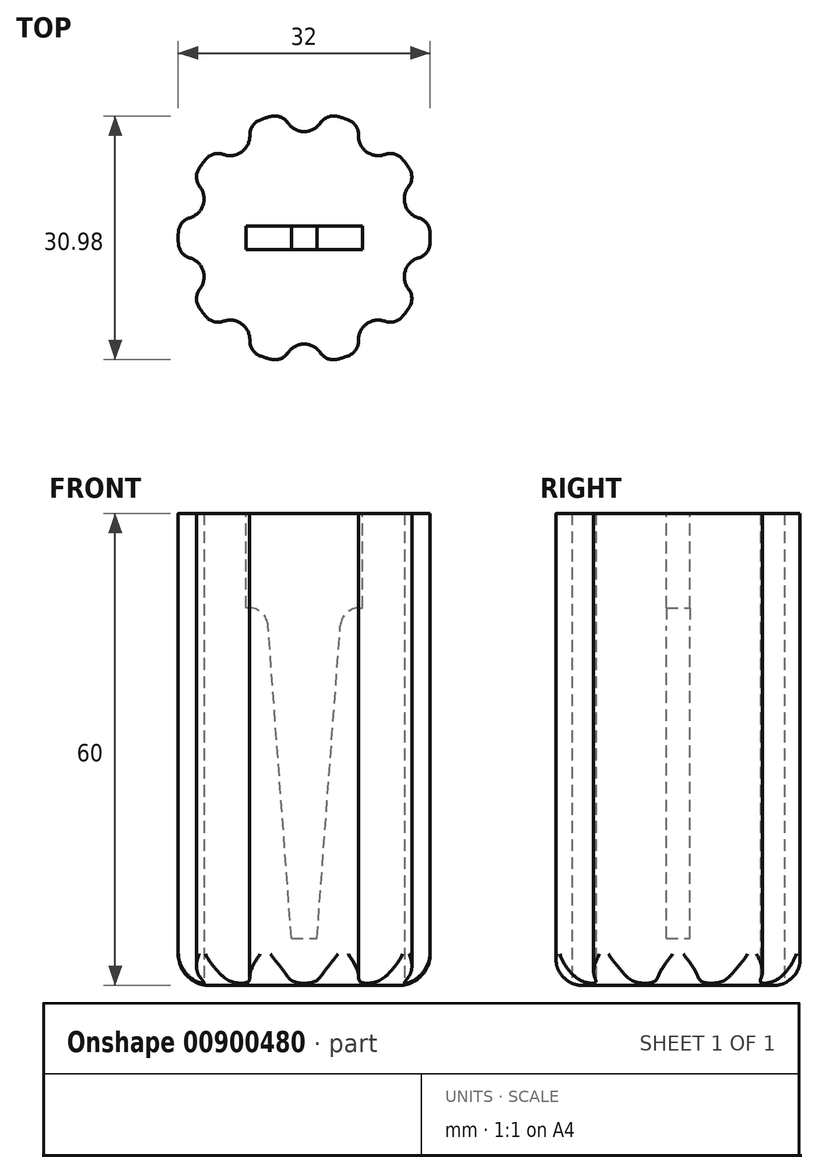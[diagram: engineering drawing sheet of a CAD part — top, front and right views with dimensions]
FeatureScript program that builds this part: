
annotation { "Feature Type Name" : "Feature", "Feature Type Description" : "" }
export const myFeature = defineFeature(function(context is Context, id is Id, definition is map)
    precondition{}
    {
        {
            var Q0;
            Q0=qCreatedBy(makeId("Top.planeOp"),FACE);
            var sketch = newSketch(context, id + "F0", { "sketchPlane" : qUnion([Q0])});
            skArc(sketch, "E0", {"start": v(-4.27, 15.42) * mm, "mid": v(-4.94, 15.22) * mm, "end": v(-5.6, 14.98) * mm});
            skArc(sketch, "E1", {"start": v(-2.08, 14.6) * mm, "mid": v(0, 13.5) * mm, "end": v(2.08, 14.6) * mm});
            skPoint(sketch, "E2.visualSharp", {"position": v(-2.5, 15.8) * mm});
            skArc(sketch, "E2.filletArc", {"start": v(-2.08, 14.6) * mm, "mid": v(-3.04, 15.37) * mm, "end": v(-4.27, 15.42) * mm});
            skPoint(sketch, "E3.visualSharp", {"position": v(2.5, 15.8) * mm});
            skArc(sketch, "E3.filletArc", {"start": v(4.27, 15.42) * mm, "mid": v(3.04, 15.37) * mm, "end": v(2.08, 14.6) * mm});
            skArc(sketch, "E4.1.0", {"start": v(-10.26, 10.6) * mm, "mid": v(-11.5, 10.64) * mm, "end": v(-12.52, 9.96) * mm});
            skArc(sketch, "E4.1.1", {"start": v(-10.26, 10.6) * mm, "mid": v(-7.94, 10.92) * mm, "end": v(-6.9, 13.04) * mm});
            skArc(sketch, "E4.1.2", {"start": v(-5.6, 14.98) * mm, "mid": v(-6.57, 14.22) * mm, "end": v(-6.9, 13.04) * mm});
            skArc(sketch, "E4.2.0", {"start": v(-14.53, 2.54) * mm, "mid": v(-15.56, 1.86) * mm, "end": v(-15.98, 0.7) * mm});
            skArc(sketch, "E4.2.1", {"start": v(-14.53, 2.54) * mm, "mid": v(-12.84, 4.17) * mm, "end": v(-13.25, 6.49) * mm});
            skArc(sketch, "E4.2.2", {"start": v(-13.35, 8.83) * mm, "mid": v(-13.68, 7.64) * mm, "end": v(-13.25, 6.49) * mm});
            skArc(sketch, "E4.3.0", {"start": v(-13.25, -6.49) * mm, "mid": v(-13.68, -7.64) * mm, "end": v(-13.35, -8.83) * mm});
            skArc(sketch, "E4.3.1", {"start": v(-13.25, -6.49) * mm, "mid": v(-12.84, -4.17) * mm, "end": v(-14.53, -2.54) * mm});
            skArc(sketch, "E4.3.2", {"start": v(-15.98, -0.7) * mm, "mid": v(-15.56, -1.86) * mm, "end": v(-14.53, -2.54) * mm});
            skArc(sketch, "E4.4.0", {"start": v(-6.9, -13.04) * mm, "mid": v(-6.57, -14.22) * mm, "end": v(-5.6, -14.98) * mm});
            skArc(sketch, "E4.4.1", {"start": v(-6.9, -13.04) * mm, "mid": v(-7.94, -10.92) * mm, "end": v(-10.26, -10.6) * mm});
            skArc(sketch, "E4.4.2", {"start": v(-12.52, -9.96) * mm, "mid": v(-11.5, -10.64) * mm, "end": v(-10.26, -10.6) * mm});
            skArc(sketch, "E4.5.0", {"start": v(2.08, -14.6) * mm, "mid": v(3.04, -15.37) * mm, "end": v(4.27, -15.42) * mm});
            skArc(sketch, "E4.5.1", {"start": v(2.08, -14.6) * mm, "mid": v(0, -13.5) * mm, "end": v(-2.08, -14.6) * mm});
            skArc(sketch, "E4.5.2", {"start": v(-4.27, -15.42) * mm, "mid": v(-3.04, -15.37) * mm, "end": v(-2.08, -14.6) * mm});
            skArc(sketch, "E4.6.0", {"start": v(10.26, -10.6) * mm, "mid": v(11.5, -10.64) * mm, "end": v(12.52, -9.96) * mm});
            skArc(sketch, "E4.6.1", {"start": v(10.26, -10.6) * mm, "mid": v(7.94, -10.92) * mm, "end": v(6.9, -13.04) * mm});
            skArc(sketch, "E4.6.2", {"start": v(5.6, -14.98) * mm, "mid": v(6.57, -14.22) * mm, "end": v(6.9, -13.04) * mm});
            skArc(sketch, "E4.7.0", {"start": v(14.53, -2.54) * mm, "mid": v(15.56, -1.86) * mm, "end": v(15.98, -0.7) * mm});
            skArc(sketch, "E4.7.1", {"start": v(14.53, -2.54) * mm, "mid": v(12.84, -4.17) * mm, "end": v(13.25, -6.49) * mm});
            skArc(sketch, "E4.7.2", {"start": v(13.35, -8.83) * mm, "mid": v(13.68, -7.64) * mm, "end": v(13.25, -6.49) * mm});
            skArc(sketch, "E4.8.0", {"start": v(13.25, 6.49) * mm, "mid": v(13.68, 7.64) * mm, "end": v(13.35, 8.83) * mm});
            skArc(sketch, "E4.8.1", {"start": v(13.25, 6.49) * mm, "mid": v(12.84, 4.17) * mm, "end": v(14.53, 2.54) * mm});
            skArc(sketch, "E4.8.2", {"start": v(15.98, 0.7) * mm, "mid": v(15.56, 1.86) * mm, "end": v(14.53, 2.54) * mm});
            skArc(sketch, "E4.9.0", {"start": v(6.9, 13.04) * mm, "mid": v(6.57, 14.22) * mm, "end": v(5.6, 14.98) * mm});
            skArc(sketch, "E4.9.1", {"start": v(6.9, 13.04) * mm, "mid": v(7.94, 10.92) * mm, "end": v(10.26, 10.6) * mm});
            skArc(sketch, "E4.9.2", {"start": v(12.52, 9.96) * mm, "mid": v(11.5, 10.64) * mm, "end": v(10.26, 10.6) * mm});
            skArc(sketch, "E5.trimOffspring", {"start": v(-15.98, 0.7) * mm, "mid": v(-16, 0) * mm, "end": v(-15.98, -0.7) * mm});
            skArc(sketch, "E6.trimOffspring", {"start": v(-12.52, 9.96) * mm, "mid": v(-12.94, 9.4) * mm, "end": v(-13.35, 8.83) * mm});
            skArc(sketch, "E7.trimOffspring", {"start": v(5.6, 14.98) * mm, "mid": v(4.94, 15.22) * mm, "end": v(4.27, 15.42) * mm});
            skArc(sketch, "E8.trimOffspring", {"start": v(13.35, 8.83) * mm, "mid": v(12.94, 9.4) * mm, "end": v(12.52, 9.96) * mm});
            skArc(sketch, "E9.trimOffspring", {"start": v(15.98, -0.7) * mm, "mid": v(16, 0) * mm, "end": v(15.98, 0.7) * mm});
            skArc(sketch, "E10.trimOffspring", {"start": v(12.52, -9.96) * mm, "mid": v(12.94, -9.4) * mm, "end": v(13.35, -8.83) * mm});
            skArc(sketch, "E11.trimOffspring", {"start": v(4.27, -15.42) * mm, "mid": v(4.94, -15.22) * mm, "end": v(5.6, -14.98) * mm});
            skArc(sketch, "E12.trimOffspring", {"start": v(-5.6, -14.98) * mm, "mid": v(-4.94, -15.22) * mm, "end": v(-4.27, -15.42) * mm});
            skArc(sketch, "E13.trimOffspring", {"start": v(-13.35, -8.83) * mm, "mid": v(-12.94, -9.4) * mm, "end": v(-12.52, -9.96) * mm});
            skSolve(sketch);
        }
        {
            var Q0;
            Q0=makeQuery(id+"F0.imprint","IMPRINT",FACE,{"disambiguationData":[TD([[makeQuery(id+"F0.imprint","IMPRINT",EDGE,{"derivedFrom":sQuery(id+"F0.wireOp",EDGE,"E0")}),1.0]])]});
            extrude(context, id + "F1", {"entities" : qUnion([Q0]), "depth" : 60 * mm, "offsetDistance" : 25.4 * mm});
        }
        {
            var Q0;
            Q0=qCreatedBy(makeId("Right.planeOp"),FACE);
            var sketch = newSketch(context, id + "F2", { "sketchPlane" : qUnion([Q0])});
            skLineSegment(sketch, "E14.bottom", {"start": v(12, 0) * mm, "end": v(16, 0) * mm});
            skLineSegment(sketch, "E14.top", {"start": v(12, 4) * mm, "end": v(16, 4) * mm});
            skLineSegment(sketch, "E14.left", {"start": v(12, 0) * mm, "end": v(12, 4) * mm});
            skLineSegment(sketch, "E14.right", {"start": v(16, 0) * mm, "end": v(16, 4) * mm});
            skArc(sketch, "E15", {"start": v(12, 0) * mm, "mid": v(14.83, 1.17) * mm, "end": v(16, 4) * mm});
            skLineSegment(sketch, "E16", {"start": v(12, 0) * mm, "end": v(0, 0) * mm});
            skLineSegment(sketch, "E17", {"start": v(0, 0) * mm, "end": v(0, 89.76) * mm});
            skSolve(sketch);
        }
        {
            var Q0;
            Q0=makeQuery(id+"F2.imprint","IMPRINT",FACE,{"disambiguationData":[TD([[makeQuery(id+"F2.imprint","IMPRINT",EDGE,{"derivedFrom":sQuery(id+"F2.wireOp",EDGE,"E14.bottom")}),1.0]])]});
            var Q1;
            Q1=sQuery(id+"F2.wireOp",EDGE,"E17");
            revolve(context, id + "F3", {"operationType" : NewBodyOperationType.REMOVE, "surfaceOperationType" : NewSurfaceOperationType.NEW, "entities" : qUnion([Q0]), "axis" : qUnion([Q1]), "revolveType" : RevolveType.FULL, "oppositeDirection" : true});
        }
        {
            var Q0;
            Q0=qCreatedBy(makeId("Front.planeOp"),FACE);
            var sketch = newSketch(context, id + "F4", { "sketchPlane" : qUnion([Q0])});
            skLineSegment(sketch, "E18", {"start": v(0, 0) * mm, "end": v(0, 6) * mm});
            skLineSegment(sketch, "E19", {"start": v(0, 6) * mm, "end": v(0, 48) * mm});
            skLineSegment(sketch, "E20", {"start": v(0, 48) * mm, "end": v(0, 60) * mm});
            skLineSegment(sketch, "E21.bottom", {"start": v(7.07, 48) * mm, "end": v(7.4, 48) * mm});
            skLineSegment(sketch, "E21.top", {"start": v(0, 60) * mm, "end": v(7.4, 60) * mm});
            skLineSegment(sketch, "E21.right", {"start": v(7.4, 48) * mm, "end": v(7.4, 60) * mm});
            skLineSegment(sketch, "E22", {"start": v(0, 6) * mm, "end": v(1.63, 6) * mm});
            skLineSegment(sketch, "E23", {"start": v(1.63, 6) * mm, "end": v(0, 6) * mm});
            skLineSegment(sketch, "E24", {"start": v(0, 48) * mm, "end": v(4.75, 48) * mm});
            skLineSegment(sketch, "E25", {"start": v(1.62, 6) * mm, "end": v(4.58, 45.69) * mm});
            skArc(sketch, "E26.filletArc", {"start": v(7.07, 48) * mm, "mid": v(5.37, 47.33) * mm, "end": v(4.58, 45.69) * mm});
            skLineSegment(sketch, "E27.MirrorCS", {"start": v(-1.62, 6) * mm, "end": v(-4.58, 45.69) * mm});
            skLineSegment(sketch, "E28.MirrorCS", {"start": v(-1.63, 6) * mm, "end": v(0, 6) * mm});
            skArc(sketch, "E29.MirrorCS", {"start": v(-7.07, 48) * mm, "mid": v(-5.37, 47.33) * mm, "end": v(-4.58, 45.69) * mm});
            skLineSegment(sketch, "E30.MirrorCS", {"start": v(-7.07, 48) * mm, "end": v(-7.4, 48) * mm});
            skLineSegment(sketch, "E31.MirrorCS", {"start": v(-7.4, 48) * mm, "end": v(-7.4, 60) * mm});
            skLineSegment(sketch, "E32.MirrorCS", {"start": v(0, 60) * mm, "end": v(-7.4, 60) * mm});
            skSolve(sketch);
        }
        {
            var Q0;
            Q0 = qSketchRegion(id + "F4", true);
            extrude(context, id + "F5", {"entities" : qUnion([Q0]), "operationType" : NewBodyOperationType.REMOVE, "endBound" : BoundingType.SYMMETRIC, "depth" : 3 * mm, "offsetDistance" : 25.4 * mm});
        }
    });
